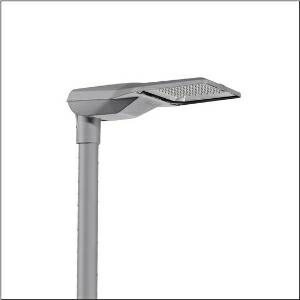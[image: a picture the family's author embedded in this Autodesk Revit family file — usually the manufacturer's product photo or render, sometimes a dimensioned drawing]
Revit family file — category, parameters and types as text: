
# Revit family: streetlight_sl_21_iq_midi___stw1_0a_5xe3e31d08mb_516a
name_source: partatom
category: Lighting Fixtures
units: mm (PartAtom-declared; Revit-internal decimal feet)

## family parameters
Cut with Voids When Loaded = No
Host = Face
Light Source = No
Part Type = Normal
Room Calculation Point = No
Round Connector Dimension = Use Diameter
Shared = No

## types (1)
- --- (1 x LED, 19500 lm, 146.7 W, 3000K)
    Apparent Load = 147 VA
    CIE Flux Codes = 38 75 98 100 100
    Color Rendering = 70
    Color Temperature = 3000K
    Default Elevation = 1800 mm
    Description = Streetlight SL 21 iQ midi, mast luminaire, primary light control with lens, of PMMA, primary optical cover: cover, of toughened safety glass, transparent, light distribution: STW1.0a, light emission: direct distribution, primary light characteristic: asymmetric, installation type: post-top, side-entry, LED, High Power LED, rated luminous flux: 19.500lm, luminous efficacy: 133lm/W, light colour: 730, colour temperature: 3000K, control gear: iQ-Comfort, control: Auto-Match, Temp-Guard, Lumen-Switch, Night-Set, Smart-Wire, Light-Fading, Desk-Remote (wireless, voltage-free reading and setting of iQ features in the workshop via application-optimized NFC function/RFID function), optimised constant luminous flux control (CLO 2.0), pre-setting: linear dimming characteristic, mains connection: 230..240V, AC, 50/60Hz, start of lifetime: 147W, end of service life: 161W, reduction: 62W, luminaire housing, of diecast aluminium, powder-coated, SITECO metallic grey (DB 702S), corrosivity category C5 high according to DIN EN ISO 12944, please order mast flange separately, inclination adjustable: 0°, 5°, 10°, 15°, sealing non-destructively replaceable, multi-level sealing system, length: 644mm, width: 335mm, height: 110mm, mast flange for spigot size: 42mm (side-entry): 5XC10008XM4, 60/48mm (side-entry/post-top): 5XC10108XM2, 76/60mm (side-entry/post-top): 5XC10108XM1, mounting height: 4..8m, protection rating (complete): IP66, insulation class (complete): insulation class II (safety insulation), certification: CE, ENEC, ENEC+, VDE, impact resistance: IK10, permissible operating ambient temperature for outdoor applications: -40..+50°C, standard-compliant lighting for roads and squares, packaging unit: 1 piece

Light Distribution: STW1.0a
    Height = 111 mm
    Lamp = 1 x LED
    Lamp Light Flux = 19500 lm
    Lamp Power = 146.7 W
    Lamp count = 1
    Length = 644 mm
    Luminous efficacy = 133 lm/W
    Manufacturer = Siteco
    ModVariant = No
    Model = 5XE3E31D08MB
    Number of Poles = 1
    OnlyDefault = Yes
    Power Factor = 1
    Product Name = Streetlight SL 21 iQ midi | STW1.0a
    Product group = mast luminaire | pylon top
    ProductGroupID = 6100
    Protection Class = Protection class II
    Protection Degree = IP 66
    RLX_Detail_Level = 1
    RLX_Emergency_Light_Flux = 0 lm
    RLX_Emergency_Type = 0
    RLX_Emergency_Type_DB = No
    RlxData = <blob elided: 26989 chars, md5=3deb2f2c>
    Socket = socket
    Standby Power = 0 W
    System Light Flux = 19499 lm
    System Power = 147 W
    Type Comments = factory setting: luminous flux: 100 % | dim-lin: 254 | 753 mA
    Type Image = l_1004298.jpg
    URL = http://relux.com
    VarID = @adj_185601
    Voltage = 0 V
    Weight = 0.00 kg
    Width = 336 mm

## geometry (parser evidence)
native form markers: Blend x4, Sweep x11
no freeform markers — native parametric forms only
